# Revit family: NLRS_57_AIR_UN_induction-unit-oknv300_LT_sacs
name_source: partatom
category: Mechanical Equipment
units: mm (PartAtom-declared; Revit-internal decimal feet)

## family parameters
Always vertical = Yes
Classification = None
Cut with Voids When Loaded = No
OmniClass Number = 23.75.00.00
OmniClass Title = Climate Control (HVAC)
Part Type = Normal
Room Calculation Point = No
Round Connector Dimension = Use Diameter
Shared = No
Work Plane-Based = No

## types (5) — shared parameters
Assembly Code = 57.00
Description = Induction unit for use in modular ceilings, Type OKNI 300 and 400
FireRating = 00
IfcDescription = Induction unit for use in modular ceilings, Type OKNI 300 and 400
IfcExportAs = IfcAirTerminalType
IfcExportType = DIFFUSER
LoadBearing = No
NLRS_C_content_datum_uitgifte = 02-06-2023
NLRS_C_content_provider = Solid Air Climate Solutions
NLRS_C_content_versie = 3.20.02
SACS_Plenum_Material = Sendzimir verzinkt
SACS_Real_Width = 595 mm  [stored 1.9521 ft]
Type Comments = Do not mirror the model!
URL = https://solid-air.nl
zero-valued in all types: Default Elevation

## per-type parameters (varying)
| type | SACS_Base_Index | SACS_Length_STD | SACS_Length_X2 | SACS_Offset1 | SACS_Offset2 | SACS_Plenum_L | SACS_Plenum_Offset |
| 300-1200 | 1 | 1195 mm  [stored 3.9206 ft] | 1140 mm  [stored 3.74016 ft] | 35 mm  [stored 0.114829 ft] | 55 mm  [stored 0.180446 ft] | 980 mm  [stored 3.21522 ft] | 580 mm  [stored 1.90289 ft] |
| 300-1500 | 3 | 1495 mm | 1440 mm  [stored 4.72441 ft] | 35 mm  [stored 0.114829 ft] | 55 mm  [stored 0.180446 ft] | 1280 mm  [stored 4.19948 ft] | 730 mm  [stored 2.39501 ft] |
| 300-1800 | 5 | 1795 mm | 1670 mm | 35 mm  [stored 0.114829 ft] | 55 mm  [stored 0.180446 ft] | 1510 mm  [stored 4.95407 ft] | 845 mm  [stored 2.77231 ft] |
| 300-2400 | 7 | 2395 mm  [stored 7.85761 ft] | 2295 mm  [stored 7.52953 ft] | 55 mm  [stored 0.180446 ft] | 35 mm  [stored 0.114829 ft] | 2110 mm  [stored 6.92257 ft] | 1170 mm  [stored 3.83858 ft] |
| 300-3000 | 9 | 2995 mm  [stored 9.82612 ft] | 2895 mm  [stored 9.49803 ft] | 55 mm  [stored 0.180446 ft] | 35 mm  [stored 0.114829 ft] | 2710 mm  [stored 8.89108 ft] | 1470 mm |

note: [stored X ft] marks values corroborated as IEEE doubles in the binary element streams (Revit-internal decimal feet)

## geometry (parser evidence)
native form markers: Sweep x16
no freeform markers — native parametric forms only
